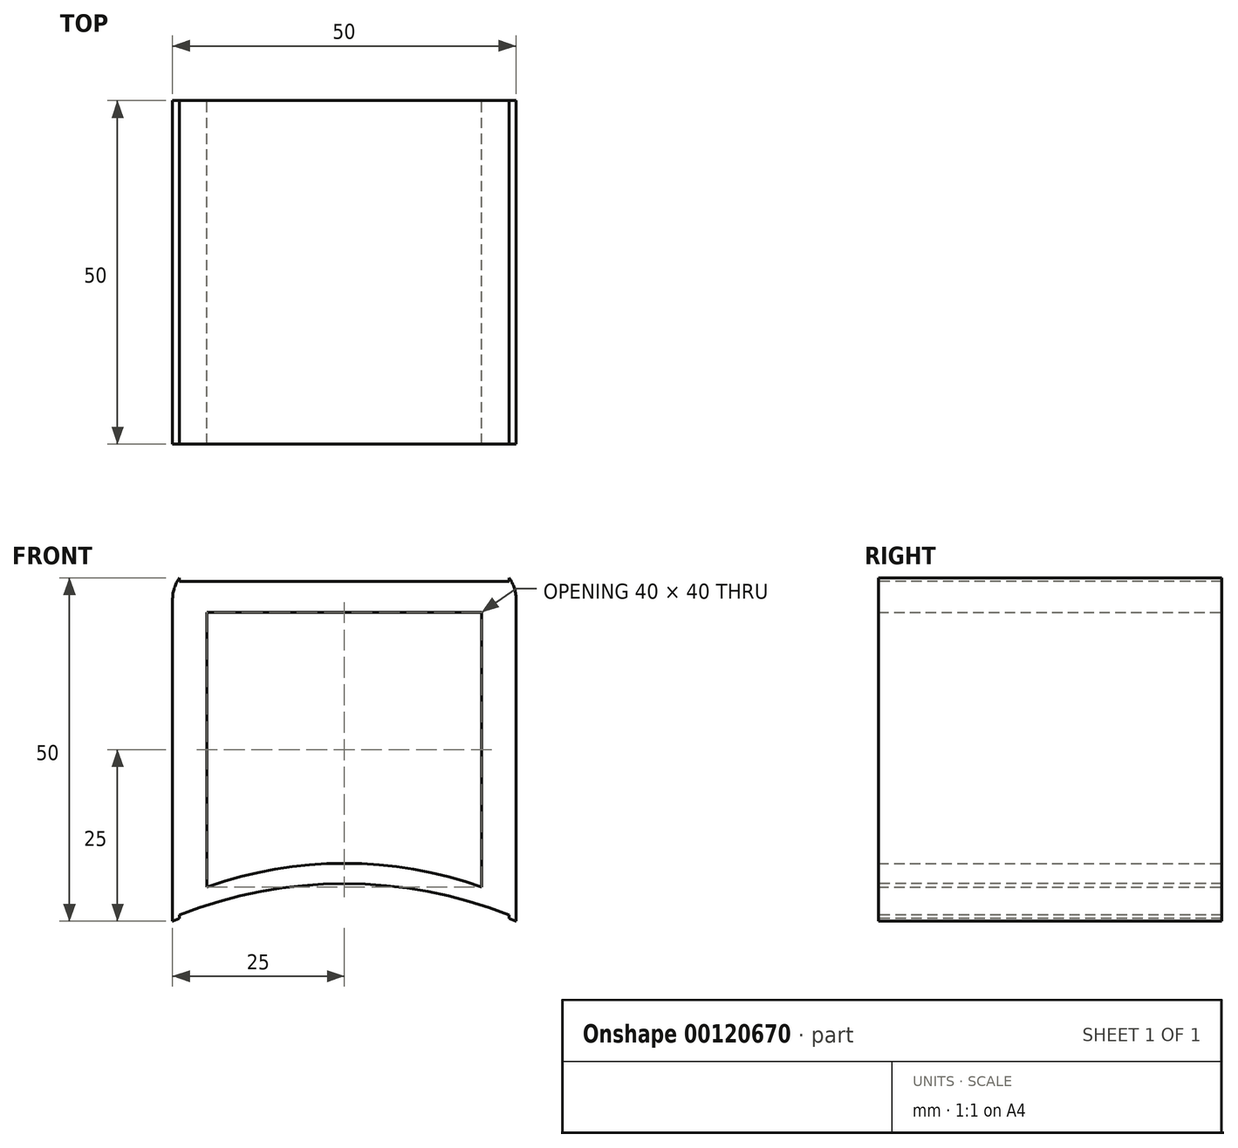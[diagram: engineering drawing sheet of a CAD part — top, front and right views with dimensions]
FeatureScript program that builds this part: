
annotation { "Feature Type Name" : "Feature", "Feature Type Description" : "" }
export const myFeature = defineFeature(function(context is Context, id is Id, definition is map)
    precondition{}
    {
        {
            var Q0;
            Q0=qCreatedBy(makeId("Front.planeOp"),FACE);
            var sketch = newSketch(context, id + "F0", { "sketchPlane" : qUnion([Q0])});
            skLineSegment(sketch, "E0.top", {"start": v(25, 25) * mm, "end": v(-25, 25) * mm});
            skLineSegment(sketch, "E0.left", {"start": v(25, -25) * mm, "end": v(25, 25) * mm});
            skLineSegment(sketch, "E0.right", {"start": v(-25, -25) * mm, "end": v(-25, 25) * mm});
            skPoint(sketch, "E0.middle", {"position": v(0, 0) * mm});
            skLineSegment(sketch, "E1.top", {"start": v(20, 20) * mm, "end": v(-20, 20) * mm});
            skLineSegment(sketch, "E1.left", {"start": v(20, -20) * mm, "end": v(20, 20) * mm});
            skLineSegment(sketch, "E1.right", {"start": v(-20, -20) * mm, "end": v(-20, 20) * mm});
            skArc(sketch, "E2", {"start": v(25, -25) * mm, "mid": v(0, -20) * mm, "end": v(-25, -25) * mm});
            skArc(sketch, "E3", {"start": v(20, -20) * mm, "mid": v(0, -16.57) * mm, "end": v(-20, -20) * mm});
            skSolve(sketch);
        }
        {
            var Q0;
            Q0=makeQuery(id+"F0.imprint","IMPRINT",FACE,{"disambiguationData":[TD([[makeQuery(id+"F0.imprint","IMPRINT",EDGE,{"derivedFrom":sQuery(id+"F0.wireOp",EDGE,"E0.top")}),1.0]])]});
            extrude(context, id + "F1", {"entities" : qUnion([Q0]), "depth" : 50 * mm});
        }
        {
            var Q0;
            Q0=makeQuery(id+"F1.opExtrude","CAP_FACE",FACE,{"disambiguationData":[OSD([sQuery(id+"F0.wireOp",EDGE,"E0.top"),sQuery(id+"F0.wireOp",EDGE,"E0.left"),sQuery(id+"F0.wireOp",EDGE,"E0.right"),sQuery(id+"F0.wireOp",EDGE,"E1.top"),sQuery(id+"F0.wireOp",EDGE,"E1.left"),sQuery(id+"F0.wireOp",EDGE,"E1.right"),sQuery(id+"F0.wireOp",EDGE,"E2"),sQuery(id+"F0.wireOp",EDGE,"E3")])],"isStart":false});
            var sketch = newSketch(context, id + "F2", { "sketchPlane" : qUnion([Q0])});
            skLineSegment(sketch, "E4", {"start": v(-24, -24.6) * mm, "end": v(-24, -24.1) * mm});
            skLineSegment(sketch, "E5", {"start": v(24, -24.6) * mm, "end": v(24, -24.1) * mm});
            skArc(sketch, "E6", {"start": v(24, -24.1) * mm, "mid": v(0, -19.54) * mm, "end": v(-24, -24.1) * mm});
            skArc(sketch, "E7", {"start": v(24, -24.6) * mm, "mid": v(0, -20) * mm, "end": v(-24, -24.6) * mm});
            skLineSegment(sketch, "E8.bottom", {"start": v(-24, 26.5) * mm, "end": v(24, 26.5) * mm});
            skLineSegment(sketch, "E8.top", {"start": v(-24, 24.5) * mm, "end": v(24, 24.5) * mm});
            skLineSegment(sketch, "E8.left", {"start": v(-24, 26.5) * mm, "end": v(-24, 24.5) * mm});
            skLineSegment(sketch, "E8.right", {"start": v(24, 26.5) * mm, "end": v(24, 24.5) * mm});
            skSolve(sketch);
        }
        {
            var Q0;
            {var subQ0=sQuery(id+"F2.wireOp",EDGE,"E8.top");Q0=makeQuery(id+"F2.imprint","IMPRINT",FACE,{"disambiguationData":[TD([[makeQuery(id+"F2.imprint","IMPRINT",EDGE,{"derivedFrom":subQ0}),1.0]])]});}
            var Q1;
            {var subQ0=sQuery(id+"F2.wireOp",EDGE,"E8.bottom");Q1=makeQuery(id+"F2.imprint","IMPRINT",FACE,{"disambiguationData":[TD([[makeQuery(id+"F2.imprint","IMPRINT",EDGE,{"derivedFrom":subQ0}),-1.0]])]});}
            var Q2;
            Q2=makeQuery(id+"F2.imprint","IMPRINT",FACE,{"disambiguationData":[TD([[makeQuery(id+"F2.imprint","IMPRINT",EDGE,{"derivedFrom":sQuery(id+"F2.wireOp",EDGE,"E4")}),-1.0]])]});
            extrude(context, id + "F3", {"entities" : qUnion([Q0, Q1, Q2]), "operationType" : NewBodyOperationType.REMOVE, "oppositeDirection" : true, "depth" : 50 * mm});
        }
        {
            var Q0;
            Q0=makeQuery(id+"F1.opExtrude","SWEPT_EDGE",EDGE,{"disambiguationData":[OSD([sQuery(id+"F0.wireOp",EDGE,"E0.top"),sQuery(id+"F0.wireOp",EDGE,"E0.left")])]});
            var Q1;
            Q1=makeQuery(id+"F1.opExtrude","SWEPT_EDGE",EDGE,{"disambiguationData":[OSD([sQuery(id+"F0.wireOp",EDGE,"E0.top"),sQuery(id+"F0.wireOp",EDGE,"E0.right")])]});
            fillet(context, id + "F4", {"entities" : qUnion([Q0, Q1]), "radius" : 5.08 * mm, "tangentPropagation" : true, "allowEdgeOverflow" : false});
        }
    });
